# Revit family: Pilona BAR atornillable
name_source: partatom
category: Furniture
units: mm (PartAtom-declared; Revit-internal decimal feet)

## family parameters
Always vertical = Yes
Cut with Voids When Loaded = No
OmniClass Number = 23.40.20.00
OmniClass Title = General Furniture and Specialties
Room Calculation Point = No
Shared = No
Work Plane-Based = No

## types (1)
- Pilona BAR atornillable-H414VA-80mm
    A = 0.08 m
    B = 0.16 m
    Default Elevation = 0 m
    Description = Pilona fabricada en poliuretano, con placa de refuerzo en acero inoxidable
    Fabricante = BENITO URBAN SL
    Ficha_Tecnica = https://www.benito.com
    H = 0.87 m
    Material = Polyurethane
    Referencia = H414VA
    Type Comments = Absorbe cualquier impacto de vehículos y recupera la verticalidad al 100%. Supera una flexión de 1500 ciclos a 45º y 50 ciclos a 90º, sin daños. Clasificación “E” de comportamiento al fuego, según norma UNE-EN
13501-1:2007+A1:2010. Resistente a -50º según norma UNE ISO 812.
    URL_Producto = https://www.benito.com

## geometry (parser evidence)
native form markers: Blend x8, Sweep x2
no freeform markers — native parametric forms only
